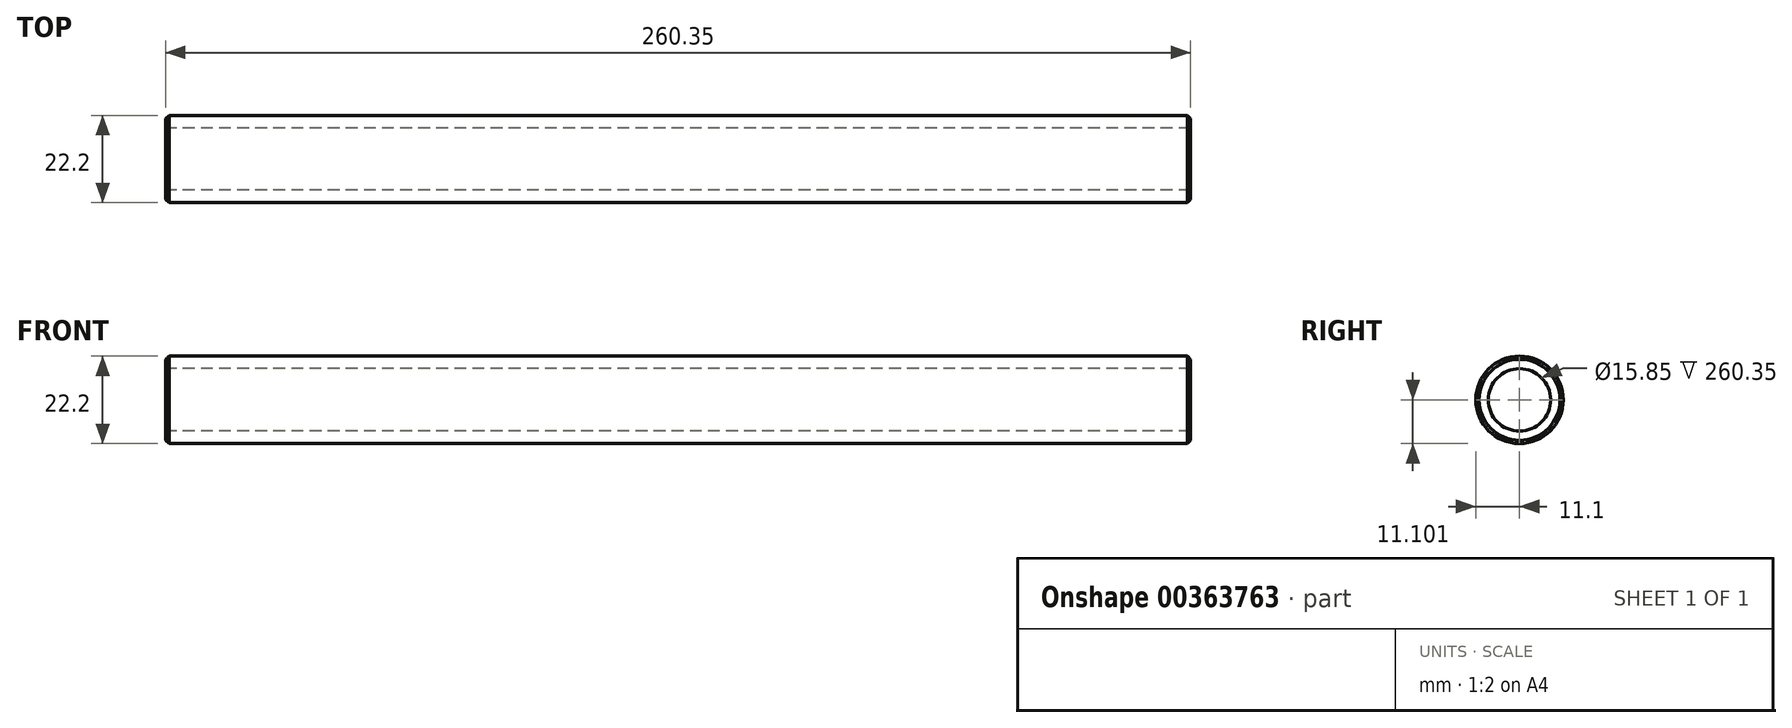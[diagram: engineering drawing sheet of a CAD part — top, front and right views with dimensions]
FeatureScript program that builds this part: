
annotation { "Feature Type Name" : "Feature", "Feature Type Description" : "" }
export const myFeature = defineFeature(function(context is Context, id is Id, definition is map)
    precondition{}
    {
        {
            var Q0;
            Q0=qCreatedBy(makeId("Front.planeOp"),FACE);
            var sketch = newSketch(context, id + "F0", { "sketchPlane" : qUnion([Q0])});
            skLineSegment(sketch, "E0", {"start": v(-138.46, 1.62) * mm, "end": v(121.9, 1.62) * mm});
            skLineSegment(sketch, "E1", {"start": v(121.9, 1.62) * mm, "end": v(121.9, -1.55) * mm});
            skLineSegment(sketch, "E2", {"start": v(121.9, -1.55) * mm, "end": v(-138.46, -1.55) * mm});
            skLineSegment(sketch, "E3", {"start": v(-138.46, -1.55) * mm, "end": v(-138.46, 1.62) * mm});
            skLineSegment(sketch, "E4", {"start": v(-138.46, -9.48) * mm, "end": v(121.9, -9.48) * mm, "construction": true});
            skLineSegment(sketch, "E5", {"start": v(109.2, -1.55) * mm, "end": v(109.2, 1.62) * mm});
            skLineSegment(sketch, "E6", {"start": v(-5.1, -1.55) * mm, "end": v(-5.1, 1.62) * mm});
            skSolve(sketch);
        }
        {
            var Q0;
            {var subQ0=sQuery(id+"F0.wireOp",EDGE,"E3");Q0=makeQuery(id+"F0.imprint","IMPRINT",FACE,{"disambiguationData":[TD([[makeQuery(id+"F0.imprint","IMPRINT",EDGE,{"derivedFrom":subQ0}),-1.0]])]});}
            var Q1;
            {var subQ0=sQuery(id+"F0.wireOp",EDGE,"E1");Q1=makeQuery(id+"F0.imprint","IMPRINT",FACE,{"disambiguationData":[TD([[makeQuery(id+"F0.imprint","IMPRINT",EDGE,{"derivedFrom":subQ0}),-1.0]])]});}
            var Q2;
            {var subQ0=sQuery(id+"F0.wireOp",EDGE,"E5");Q2=makeQuery(id+"F0.imprint","IMPRINT",FACE,{"disambiguationData":[TD([[makeQuery(id+"F0.imprint","IMPRINT",EDGE,{"derivedFrom":subQ0}),1.0]])]});}
            var Q3;
            Q3=sQuery(id+"F0.wireOp",EDGE,"E4");
            revolve(context, id + "F1", {"entities" : qUnion([Q0, Q1, Q2]), "axis" : qUnion([Q3]), "revolveType" : RevolveType.FULL});
        }
        {
            var Q0;
            Q0=makeQuery(id+"F1.opRevolve","SWEPT_EDGE",EDGE,{"disambiguationData":[OSD([sQuery(id+"F0.wireOp",EDGE,"E0"),sQuery(id+"F0.wireOp",EDGE,"E1")])]});
            chamfer(context, id + "F2", {"entities" : qUnion([Q0]), "width" : 0.81 * mm, "tangentPropagation" : true});
        }
        {
            var Q0;
            Q0=makeQuery(id+"F1.opRevolve","SWEPT_EDGE",EDGE,{"disambiguationData":[OSD([sQuery(id+"F0.wireOp",EDGE,"E0"),sQuery(id+"F0.wireOp",EDGE,"E3")])]});
            chamfer(context, id + "F3", {"entities" : qUnion([Q0]), "width" : 0.81 * mm, "tangentPropagation" : true});
        }
    });
